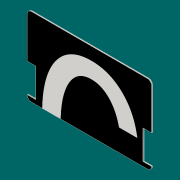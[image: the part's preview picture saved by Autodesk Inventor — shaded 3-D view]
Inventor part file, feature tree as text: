
AUTODESK INVENTOR PART (.ipt)
format: ipt  version: 2016 (Build 200138000, 138)  size: 219,648 bytes
history: native  units: mm
features: sketch x5, extrude x3, projected_geometry x3, other x2, fillet x1, mirror x1
ambient origin geometry x8: Origin, YZ Plane, XZ Plane, XY Plane, X Axis, Y Axis, Z Axis, Center Point
bodies: Solid1 (feature_tree)
feature tree (15):
  extrude  "Extrusion1"  Depth=53.98mm
  fillet  "Fillet1"  Radius=0.76mm
  extrude  "Extrusion2"  Depth=2.88mm
  extrude  "Extrusion3"  Depth=5.588mm
  mirror  "Mirror1"
  other  "Decal1"
  other  "Decal2"
  sketch  "Sketch1"  dims[d0=85.6mm d1=53.98mm d2=0.76mm]
  sketch  "Sketch2"  dims[d3=0.0mm d4=2.88mm]
  projected_geometry  "Projected Loop1"
  sketch  "Sketch3"  dims[d5=5.588mm d6=5.588mm]
  sketch  "Sketch4"  dims[d7=3.0mm]
  projected_geometry  "Projected Loop2"
  sketch  "Sketch5"  dims[d8=3.0mm d9=20.0mm d10=20.0mm d11=0.76mm d12=0.0mm d13=3.0mm d14=3.0mm d15=0.76mm d16=1.5mm d17=1.5mm d18=1.5mm d19=0.76mm d20=0.0mm]
  projected_geometry  "Projected Loop3"
